# Revit family: 2Celite_Acesso_Bacia com Caixa Acoplada_31359
name_source: partatom
category: Plumbing Fixtures
revit_build: Autodesk Revit MEP 2014 (Build: 20131024_2115(x64)
units: mm (PartAtom-declared; Revit-internal decimal feet)

## types (1)
- Branca - 31359 com Caixa e Assento Plus PP
    Assembly Code = D2010100
    CWFU = 1
    Celite: Categoria = Linhas Completas
    Celite: Cores Disponíveis = Branco
    Celite: Código = 31359
    Celite: Descrição = Bacia com caixa acoplada 3 e 6 litros cor branca (31359), assento Plus PP, linha Acesso - Louças Celite
    Celite: Desenho Técnico = http://www.celite.com.br
    Celite: Fabricante = Celite
    Celite: Linha = Acesso
    Celite: Link do Produto = http://www.celite.com.br
    Celite: Norma = ABNT NBR 15097-1:2011/ABNT NBR 15097-2:2011 - fabricação/instalação
    Celite: Produto = Louças
    Celite: Tipo = Bacias com caixas
    Celite: Versão = Autodesk Revit MEP 2014
    Default Elevation = 0 m
    Description = Bacia com caixa acoplada 3 e 6 litros cor branca (31359), assento Plus PP, linha Acesso - Louças Celite
    Desenvolvido por = ofcdesk
    Diâmetro Ponto de Esgoto = 100 mm
    Manufacturer = Celite
    Model = 31359
    Raio Ponto de Esgoto = 50 mm
    Raio Ponto de Água = 10 mm
    Selo de Qualidade ofcdesk = Standard
    Tipo de assento = Celite_Acesso_Assento para Bacia Sanitária_31981 : Branco - 31981
    Tipo de caixa = Celite_Acesso_Caixa para Acoplar_31570 : Branco - 31570
    URL = http://www.celite.com.br
    WFU = 3

## geometry (parser evidence)
native form markers: Sweep x4
no freeform markers — native parametric forms only
